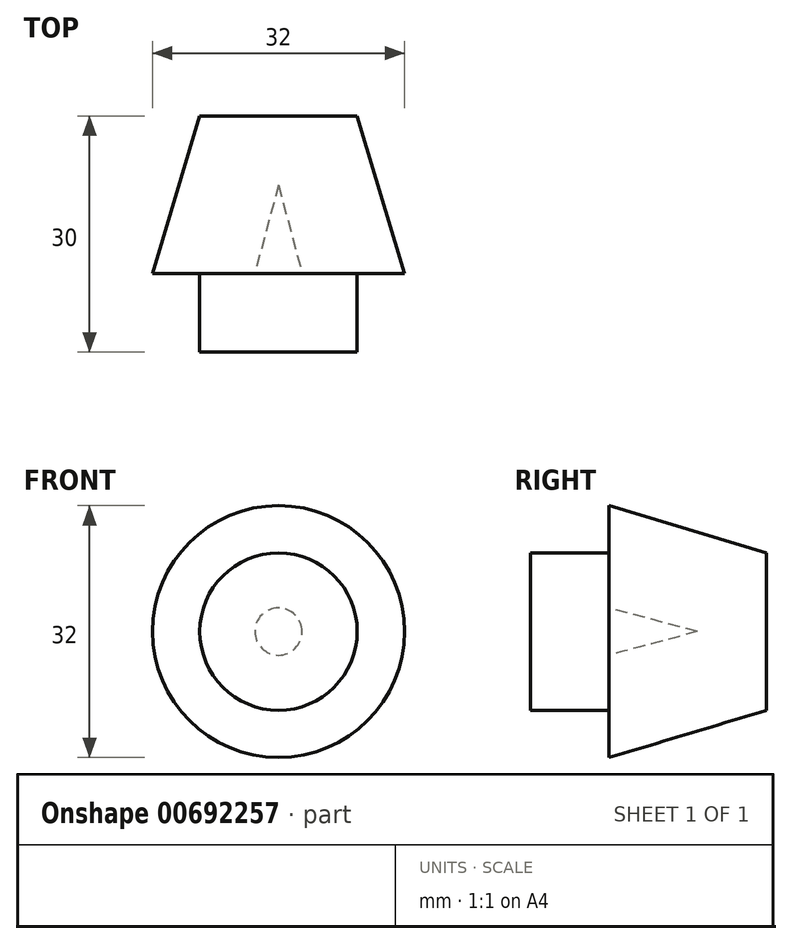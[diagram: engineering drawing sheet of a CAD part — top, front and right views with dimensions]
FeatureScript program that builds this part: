
annotation { "Feature Type Name" : "Feature", "Feature Type Description" : "" }
export const myFeature = defineFeature(function(context is Context, id is Id, definition is map)
    precondition{}
    {
        {
            var Q0;
            Q0=qCreatedBy(makeId("Top.planeOp"),FACE);
            var sketch = newSketch(context, id + "F0", { "sketchPlane" : qUnion([Q0])});
            skLineSegment(sketch, "E0", {"start": v(10, -1.19) * mm, "end": v(16, -21.19) * mm});
            skLineSegment(sketch, "E1", {"start": v(16, -21.19) * mm, "end": v(10, -21.19) * mm});
            skLineSegment(sketch, "E2", {"start": v(10, -21.19) * mm, "end": v(10, -31.19) * mm});
            skLineSegment(sketch, "E3", {"start": v(10, -31.19) * mm, "end": v(0, -31.19) * mm});
            skLineSegment(sketch, "E4", {"start": v(10, -1.19) * mm, "end": v(0, -1.19) * mm});
            skLineSegment(sketch, "E5", {"start": v(10, -21.19) * mm, "end": v(3, -21.19) * mm});
            skLineSegment(sketch, "E6", {"start": v(3, -21.19) * mm, "end": v(0, -10) * mm});
            skLineSegment(sketch, "E7", {"start": v(0, -10) * mm, "end": v(0, -1.19) * mm});
            skLineSegment(sketch, "E8", {"start": v(0, -10) * mm, "end": v(0, -31.19) * mm});
            skSolve(sketch);
        }
        {
            var Q0;
            Q0=makeQuery(id+"F0.imprint","IMPRINT",FACE,{"disambiguationData":[TD([[makeQuery(id+"F0.imprint","IMPRINT",EDGE,{"derivedFrom":sQuery(id+"F0.wireOp",EDGE,"E0")}),-1.0]])]});
            var Q1;
            Q1=sQuery(id+"F0.wireOp",EDGE,"E7");
            revolve(context, id + "F1", {"entities" : qUnion([Q0]), "axis" : qUnion([Q1]), "revolveType" : RevolveType.FULL});
        }
        {
            var Q0;
            Q0=makeQuery(id+"F0.imprint","IMPRINT",FACE,{"disambiguationData":[TD([[makeQuery(id+"F0.imprint","IMPRINT",EDGE,{"derivedFrom":sQuery(id+"F0.wireOp",EDGE,"E0")}),-1.0]])]});
            var Q1;
            Q1=makeQuery(id+"F0.imprint","IMPRINT",FACE,{"disambiguationData":[TD([[makeQuery(id+"F0.imprint","IMPRINT",EDGE,{"derivedFrom":sQuery(id+"F0.wireOp",EDGE,"E2")}),-1.0]])]});
            var Q2;
            Q2=sQuery(id+"F0.wireOp",EDGE,"E7");
            revolve(context, id + "F2", {"entities" : qUnion([Q0, Q1]), "axis" : qUnion([Q2]), "revolveType" : RevolveType.FULL});
        }
    });
